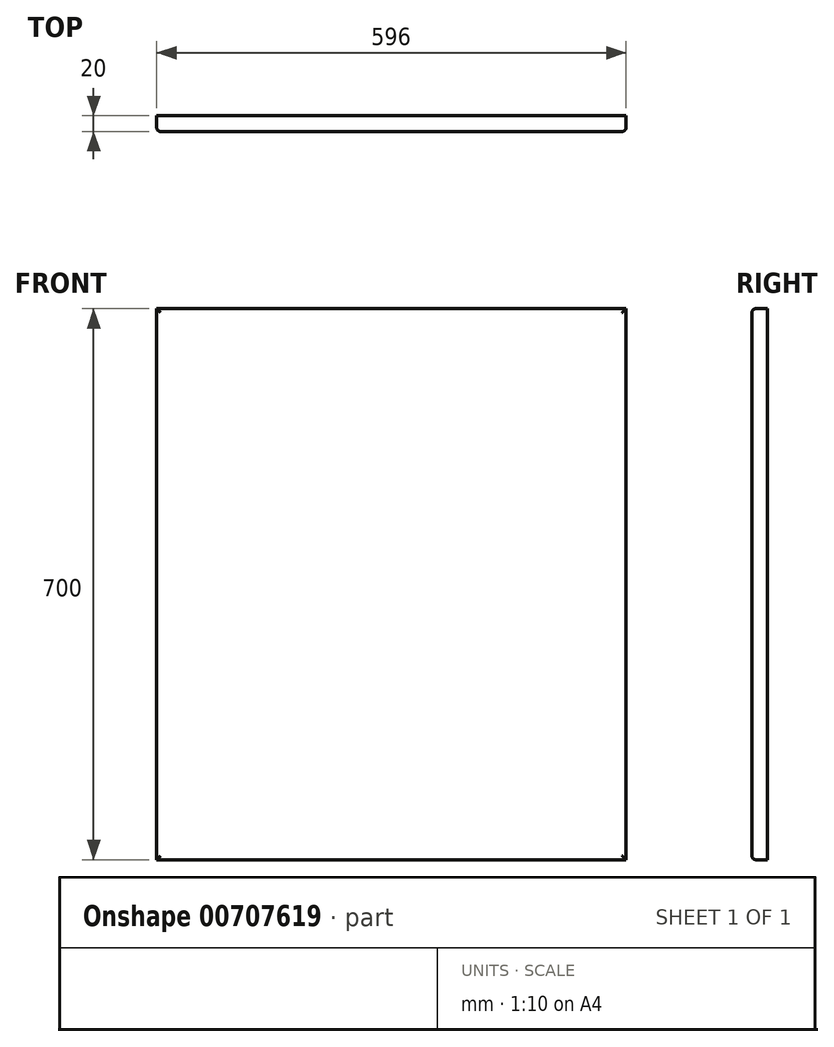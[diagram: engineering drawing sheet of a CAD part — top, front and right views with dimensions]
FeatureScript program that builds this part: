
annotation { "Feature Type Name" : "Feature", "Feature Type Description" : "" }
export const myFeature = defineFeature(function(context is Context, id is Id, definition is map)
    precondition{}
    {
        {
            var Q0;
            Q0=qCreatedBy(makeId("Front.planeOp"),FACE);
            var sketch = newSketch(context, id + "F0", { "sketchPlane" : qUnion([Q0])});
            skLineSegment(sketch, "E0.bottom", {"start": v(-315.35, 262.1) * mm, "end": v(280.65, 262.1) * mm});
            skLineSegment(sketch, "E0.top", {"start": v(-315.35, -437.9) * mm, "end": v(280.65, -437.9) * mm});
            skLineSegment(sketch, "E0.left", {"start": v(-315.35, 262.1) * mm, "end": v(-315.35, -437.9) * mm});
            skLineSegment(sketch, "E0.right", {"start": v(280.65, 262.1) * mm, "end": v(280.65, -437.9) * mm});
            skSolve(sketch);
        }
        {
            var Q0;
            Q0=makeQuery(id+"F0.imprint","IMPRINT",FACE,{"disambiguationData":[TD([[makeQuery(id+"F0.imprint","IMPRINT",EDGE,{"derivedFrom":sQuery(id+"F0.wireOp",EDGE,"E0.bottom")}),-1.0]])]});
            extrude(context, id + "F1", {"entities" : qUnion([Q0]), "depth" : 20 * mm, "offsetDistance" : 25 * mm});
        }
        {
            var Q0;
            Q0=makeQuery(id+"F1.opExtrude","CAP_EDGE",EDGE,{"disambiguationData":[OSD([sQuery(id+"F0.wireOp",EDGE,"E0.bottom")])],"isStart":false});
            var Q1;
            Q1=makeQuery(id+"F1.opExtrude","CAP_EDGE",EDGE,{"disambiguationData":[OSD([sQuery(id+"F0.wireOp",EDGE,"E0.right")])],"isStart":false});
            var Q2;
            Q2=makeQuery(id+"F1.opExtrude","CAP_EDGE",EDGE,{"disambiguationData":[OSD([sQuery(id+"F0.wireOp",EDGE,"E0.top")])],"isStart":false});
            var Q3;
            Q3=makeQuery(id+"F1.opExtrude","CAP_EDGE",EDGE,{"disambiguationData":[OSD([sQuery(id+"F0.wireOp",EDGE,"E0.left")])],"isStart":false});
            fillet(context, id + "F2", {"entities" : qUnion([Q0, Q1, Q2, Q3]), "radius" : 5 * mm, "tangentPropagation" : true, "allowEdgeOverflow" : false});
        }
    });
